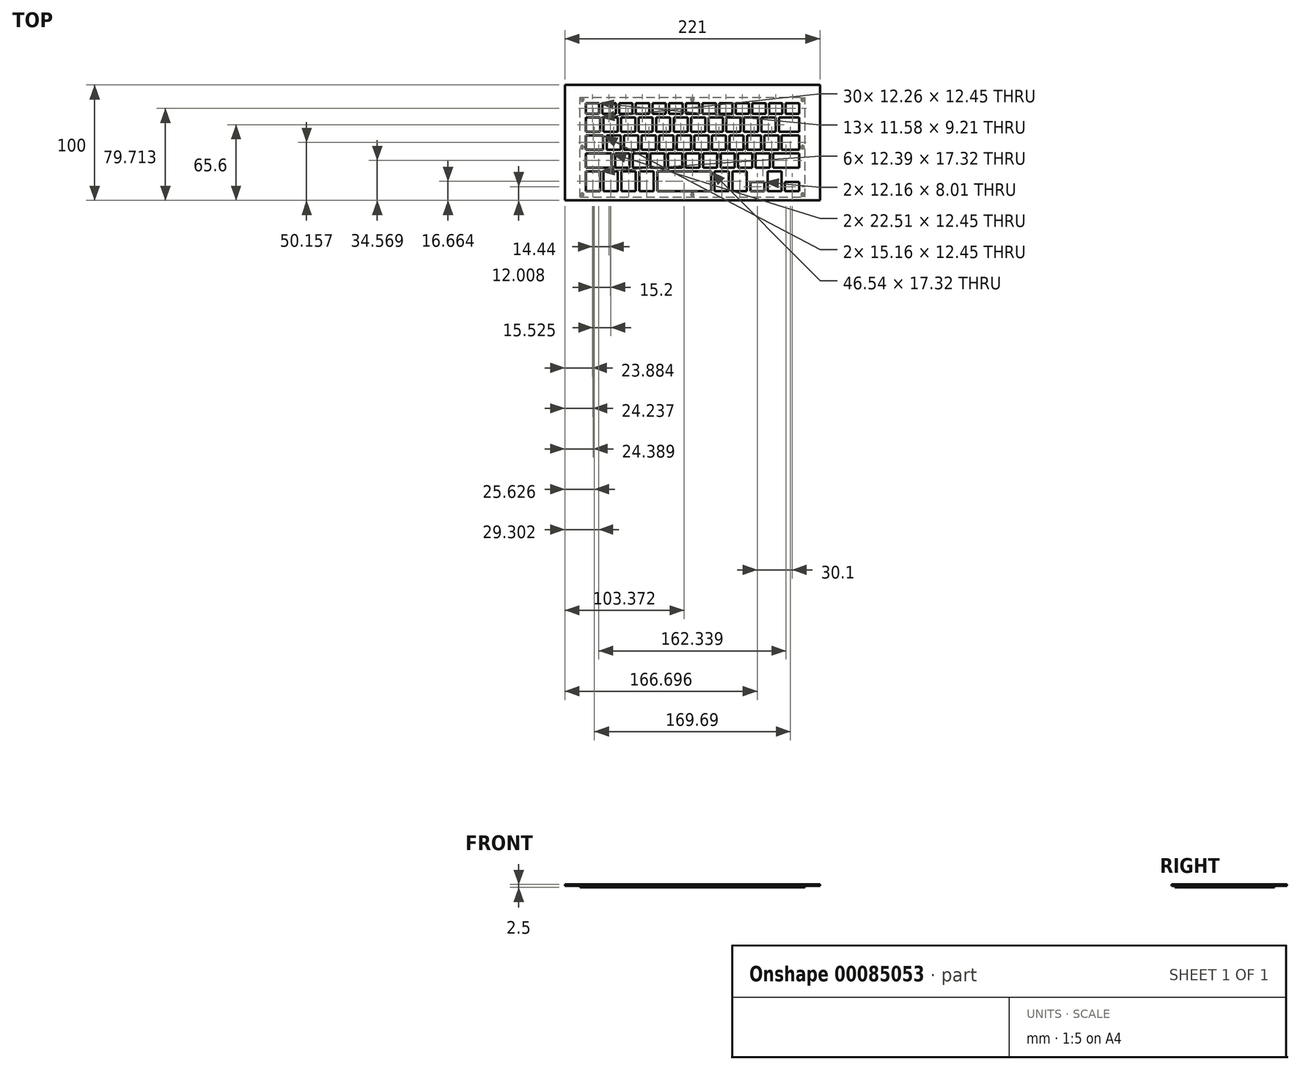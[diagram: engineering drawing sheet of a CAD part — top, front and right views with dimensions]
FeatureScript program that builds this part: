
annotation { "Feature Type Name" : "Feature", "Feature Type Description" : "" }
export const myFeature = defineFeature(function(context is Context, id is Id, definition is map)
    precondition{}
    {
        {
            var Q0;
            Q0=qCreatedBy(makeId("Top.planeOp"),FACE);
            var sketch = newSketch(context, id + "F0", { "sketchPlane" : qUnion([Q0])});
            skLineSegment(sketch, "E0", {"start": v(-92.4, 38.16) * mm, "end": v(-80.82, 38.16) * mm});
            skLineSegment(sketch, "E1", {"start": v(-92.4, 28.95) * mm, "end": v(-92.4, 38.16) * mm});
            skLineSegment(sketch, "E2", {"start": v(-80.82, 38.16) * mm, "end": v(-80.82, 28.95) * mm});
            skLineSegment(sketch, "E3", {"start": v(-80.82, 28.95) * mm, "end": v(-92.4, 28.95) * mm});
            skLineSegment(sketch, "E4", {"start": v(-77.97, 28.95) * mm, "end": v(-77.97, 38.16) * mm});
            skLineSegment(sketch, "E5", {"start": v(-66.38, 28.95) * mm, "end": v(-77.97, 28.95) * mm});
            skLineSegment(sketch, "E6", {"start": v(-66.38, 38.16) * mm, "end": v(-66.38, 28.95) * mm});
            skLineSegment(sketch, "E7", {"start": v(-77.97, 38.16) * mm, "end": v(-66.38, 38.16) * mm});
            skLineSegment(sketch, "E8", {"start": v(-63.53, 38.16) * mm, "end": v(-51.94, 38.16) * mm});
            skLineSegment(sketch, "E9", {"start": v(-63.53, 28.95) * mm, "end": v(-63.53, 38.16) * mm});
            skLineSegment(sketch, "E10", {"start": v(-51.94, 28.95) * mm, "end": v(-63.53, 28.95) * mm});
            skLineSegment(sketch, "E11", {"start": v(-51.94, 38.16) * mm, "end": v(-51.94, 28.95) * mm});
            skLineSegment(sketch, "E12", {"start": v(-49.09, 28.95) * mm, "end": v(-49.09, 38.16) * mm});
            skLineSegment(sketch, "E13", {"start": v(-37.5, 28.95) * mm, "end": v(-49.09, 28.95) * mm});
            skLineSegment(sketch, "E14", {"start": v(-37.5, 38.16) * mm, "end": v(-37.5, 28.95) * mm});
            skLineSegment(sketch, "E15", {"start": v(-49.09, 38.16) * mm, "end": v(-37.5, 38.16) * mm});
            skLineSegment(sketch, "E16", {"start": v(-34.65, 38.16) * mm, "end": v(-23.06, 38.16) * mm});
            skLineSegment(sketch, "E17", {"start": v(-34.65, 28.95) * mm, "end": v(-34.65, 38.16) * mm});
            skLineSegment(sketch, "E18", {"start": v(-23.06, 28.95) * mm, "end": v(-34.65, 28.95) * mm});
            skLineSegment(sketch, "E19", {"start": v(-23.06, 38.16) * mm, "end": v(-23.06, 28.95) * mm});
            skLineSegment(sketch, "E20", {"start": v(-20.2, 38.16) * mm, "end": v(-8.62, 38.16) * mm});
            skLineSegment(sketch, "E21", {"start": v(-20.2, 28.95) * mm, "end": v(-20.2, 38.16) * mm});
            skLineSegment(sketch, "E22", {"start": v(-8.62, 28.95) * mm, "end": v(-20.2, 28.95) * mm});
            skLineSegment(sketch, "E23", {"start": v(-8.62, 38.16) * mm, "end": v(-8.62, 28.95) * mm});
            skLineSegment(sketch, "E24", {"start": v(-5.77, 38.16) * mm, "end": v(5.82, 38.16) * mm});
            skLineSegment(sketch, "E25", {"start": v(-5.77, 28.95) * mm, "end": v(-5.77, 38.16) * mm});
            skLineSegment(sketch, "E26", {"start": v(5.82, 28.95) * mm, "end": v(-5.77, 28.95) * mm});
            skLineSegment(sketch, "E27", {"start": v(5.82, 38.16) * mm, "end": v(5.82, 28.95) * mm});
            skLineSegment(sketch, "E28", {"start": v(8.67, 38.16) * mm, "end": v(20.26, 38.16) * mm});
            skLineSegment(sketch, "E29", {"start": v(8.67, 28.95) * mm, "end": v(8.67, 38.16) * mm});
            skLineSegment(sketch, "E30", {"start": v(20.26, 28.95) * mm, "end": v(8.67, 28.95) * mm});
            skLineSegment(sketch, "E31", {"start": v(20.26, 38.16) * mm, "end": v(20.26, 28.95) * mm});
            skLineSegment(sketch, "E32", {"start": v(23.11, 38.16) * mm, "end": v(34.7, 38.16) * mm});
            skLineSegment(sketch, "E33", {"start": v(23.11, 28.95) * mm, "end": v(23.11, 38.16) * mm});
            skLineSegment(sketch, "E34", {"start": v(34.7, 28.95) * mm, "end": v(23.11, 28.95) * mm});
            skLineSegment(sketch, "E35", {"start": v(34.7, 38.16) * mm, "end": v(34.7, 28.95) * mm});
            skLineSegment(sketch, "E36", {"start": v(37.55, 38.16) * mm, "end": v(49.14, 38.16) * mm});
            skLineSegment(sketch, "E37", {"start": v(37.55, 28.95) * mm, "end": v(37.55, 38.16) * mm});
            skLineSegment(sketch, "E38", {"start": v(49.14, 28.95) * mm, "end": v(37.55, 28.95) * mm});
            skLineSegment(sketch, "E39", {"start": v(49.14, 38.16) * mm, "end": v(49.14, 28.95) * mm});
            skLineSegment(sketch, "E40", {"start": v(52, 38.16) * mm, "end": v(63.58, 38.16) * mm});
            skLineSegment(sketch, "E41", {"start": v(52, 28.95) * mm, "end": v(52, 38.16) * mm});
            skLineSegment(sketch, "E42", {"start": v(63.58, 28.95) * mm, "end": v(52, 28.95) * mm});
            skLineSegment(sketch, "E43", {"start": v(63.58, 38.16) * mm, "end": v(63.58, 28.95) * mm});
            skLineSegment(sketch, "E44", {"start": v(66.43, 38.16) * mm, "end": v(78.02, 38.16) * mm});
            skLineSegment(sketch, "E45", {"start": v(66.43, 28.95) * mm, "end": v(66.43, 38.16) * mm});
            skLineSegment(sketch, "E46", {"start": v(78.02, 28.95) * mm, "end": v(66.43, 28.95) * mm});
            skLineSegment(sketch, "E47", {"start": v(78.02, 38.16) * mm, "end": v(78.02, 28.95) * mm});
            skLineSegment(sketch, "E48", {"start": v(80.87, 38.16) * mm, "end": v(92.46, 38.16) * mm});
            skLineSegment(sketch, "E49", {"start": v(92.46, 38.16) * mm, "end": v(92.46, 28.95) * mm});
            skLineSegment(sketch, "E50", {"start": v(80.87, 28.95) * mm, "end": v(80.87, 38.16) * mm});
            skLineSegment(sketch, "E51", {"start": v(92.46, 28.95) * mm, "end": v(80.87, 28.95) * mm});
            skLineSegment(sketch, "E52", {"start": v(-92.24, 13.22) * mm, "end": v(-92.24, 25.66) * mm});
            skLineSegment(sketch, "E53", {"start": v(-92.24, 25.66) * mm, "end": v(-79.98, 25.66) * mm});
            skLineSegment(sketch, "E54", {"start": v(-79.98, 25.66) * mm, "end": v(-79.98, 13.22) * mm});
            skLineSegment(sketch, "E55", {"start": v(-79.98, 13.22) * mm, "end": v(-92.24, 13.22) * mm});
            skLineSegment(sketch, "E56", {"start": v(-77.04, 13.22) * mm, "end": v(-77.04, 25.66) * mm});
            skLineSegment(sketch, "E57", {"start": v(-77.04, 25.66) * mm, "end": v(-64.78, 25.66) * mm});
            skLineSegment(sketch, "E58", {"start": v(-64.78, 25.66) * mm, "end": v(-64.78, 13.22) * mm});
            skLineSegment(sketch, "E59", {"start": v(-64.78, 13.22) * mm, "end": v(-77.04, 13.22) * mm});
            skLineSegment(sketch, "E60", {"start": v(-61.84, 13.22) * mm, "end": v(-61.84, 25.66) * mm});
            skLineSegment(sketch, "E61", {"start": v(-61.84, 25.66) * mm, "end": v(-49.58, 25.66) * mm});
            skLineSegment(sketch, "E62", {"start": v(-49.58, 25.66) * mm, "end": v(-49.58, 13.22) * mm});
            skLineSegment(sketch, "E63", {"start": v(-49.58, 13.22) * mm, "end": v(-61.84, 13.22) * mm});
            skLineSegment(sketch, "E64", {"start": v(-46.64, 13.22) * mm, "end": v(-46.64, 25.66) * mm});
            skLineSegment(sketch, "E65", {"start": v(-46.64, 25.66) * mm, "end": v(-34.38, 25.66) * mm});
            skLineSegment(sketch, "E66", {"start": v(-34.38, 13.22) * mm, "end": v(-46.64, 13.22) * mm});
            skLineSegment(sketch, "E67", {"start": v(-34.38, 25.66) * mm, "end": v(-34.38, 13.22) * mm});
            skLineSegment(sketch, "E68", {"start": v(-31.44, 13.22) * mm, "end": v(-31.44, 25.66) * mm});
            skLineSegment(sketch, "E69", {"start": v(-19.18, 13.22) * mm, "end": v(-31.44, 13.22) * mm});
            skLineSegment(sketch, "E70", {"start": v(-19.18, 25.66) * mm, "end": v(-19.18, 13.22) * mm});
            skLineSegment(sketch, "E71", {"start": v(-31.44, 25.66) * mm, "end": v(-19.18, 25.66) * mm});
            skLineSegment(sketch, "E72", {"start": v(-16.24, 25.66) * mm, "end": v(-3.98, 25.66) * mm});
            skLineSegment(sketch, "E73", {"start": v(-1.04, 25.66) * mm, "end": v(11.22, 25.66) * mm});
            skLineSegment(sketch, "E74", {"start": v(14.16, 25.66) * mm, "end": v(26.42, 25.66) * mm});
            skLineSegment(sketch, "E75", {"start": v(-16.24, 13.22) * mm, "end": v(-16.24, 25.66) * mm});
            skLineSegment(sketch, "E76", {"start": v(-3.98, 25.66) * mm, "end": v(-3.98, 13.22) * mm});
            skLineSegment(sketch, "E77", {"start": v(-1.04, 13.22) * mm, "end": v(-1.04, 25.66) * mm});
            skLineSegment(sketch, "E78", {"start": v(11.22, 25.66) * mm, "end": v(11.22, 13.22) * mm});
            skLineSegment(sketch, "E79", {"start": v(14.16, 13.22) * mm, "end": v(14.16, 25.66) * mm});
            skLineSegment(sketch, "E80", {"start": v(26.42, 25.66) * mm, "end": v(26.42, 13.22) * mm});
            skLineSegment(sketch, "E81", {"start": v(26.42, 13.22) * mm, "end": v(14.16, 13.22) * mm});
            skLineSegment(sketch, "E82", {"start": v(11.22, 13.22) * mm, "end": v(-1.04, 13.22) * mm});
            skLineSegment(sketch, "E83", {"start": v(-3.98, 13.22) * mm, "end": v(-16.24, 13.22) * mm});
            skLineSegment(sketch, "E84", {"start": v(41.62, 13.22) * mm, "end": v(29.36, 13.22) * mm});
            skLineSegment(sketch, "E85", {"start": v(29.36, 13.22) * mm, "end": v(29.36, 25.66) * mm});
            skLineSegment(sketch, "E86", {"start": v(29.36, 25.66) * mm, "end": v(41.62, 25.66) * mm});
            skLineSegment(sketch, "E87", {"start": v(41.62, 25.66) * mm, "end": v(41.62, 13.22) * mm});
            skLineSegment(sketch, "E88", {"start": v(44.56, 13.22) * mm, "end": v(44.56, 25.66) * mm});
            skLineSegment(sketch, "E89", {"start": v(44.56, 25.66) * mm, "end": v(56.82, 25.66) * mm});
            skLineSegment(sketch, "E90", {"start": v(56.82, 25.66) * mm, "end": v(56.82, 13.22) * mm});
            skLineSegment(sketch, "E91", {"start": v(56.82, 13.22) * mm, "end": v(44.56, 13.22) * mm});
            skLineSegment(sketch, "E92", {"start": v(59.76, 13.22) * mm, "end": v(59.76, 25.66) * mm});
            skLineSegment(sketch, "E93", {"start": v(59.76, 25.66) * mm, "end": v(72.02, 25.66) * mm});
            skLineSegment(sketch, "E94", {"start": v(72.02, 25.66) * mm, "end": v(72.02, 13.22) * mm});
            skLineSegment(sketch, "E95", {"start": v(72.02, 13.22) * mm, "end": v(59.76, 13.22) * mm});
            skLineSegment(sketch, "E96", {"start": v(92.4, 13.22) * mm, "end": v(75.1, 13.22) * mm});
            skLineSegment(sketch, "E97", {"start": v(75.1, 13.22) * mm, "end": v(75.1, 25.66) * mm});
            skLineSegment(sketch, "E98", {"start": v(75.1, 25.66) * mm, "end": v(92.4, 25.66) * mm});
            skLineSegment(sketch, "E99", {"start": v(92.4, 25.66) * mm, "end": v(92.4, 13.22) * mm});
            skLineSegment(sketch, "E100", {"start": v(92.4, 10.22) * mm, "end": v(92.4, -2.23) * mm});
            skLineSegment(sketch, "E101", {"start": v(92.4, -5.37) * mm, "end": v(92.4, -17.81) * mm});
            skLineSegment(sketch, "E102", {"start": v(77.23, 10.22) * mm, "end": v(92.4, 10.22) * mm});
            skLineSegment(sketch, "E103", {"start": v(77.23, -2.23) * mm, "end": v(77.23, 10.22) * mm});
            skLineSegment(sketch, "E104", {"start": v(92.4, -2.23) * mm, "end": v(77.23, -2.23) * mm});
            skLineSegment(sketch, "E105", {"start": v(69.88, -5.37) * mm, "end": v(92.4, -5.37) * mm});
            skLineSegment(sketch, "E106", {"start": v(69.88, -17.81) * mm, "end": v(69.88, -5.37) * mm});
            skLineSegment(sketch, "E107", {"start": v(92.4, -17.81) * mm, "end": v(69.88, -17.81) * mm});
            skLineSegment(sketch, "E108", {"start": v(-92.46, 10.22) * mm, "end": v(-77.3, 10.22) * mm});
            skLineSegment(sketch, "E109", {"start": v(-92.46, -2.23) * mm, "end": v(-92.46, 10.22) * mm});
            skLineSegment(sketch, "E110", {"start": v(-77.3, -2.23) * mm, "end": v(-92.46, -2.23) * mm});
            skLineSegment(sketch, "E111", {"start": v(-77.3, 10.22) * mm, "end": v(-77.3, -2.23) * mm});
            skLineSegment(sketch, "E112", {"start": v(-92.46, -5.37) * mm, "end": v(-69.94, -5.37) * mm});
            skLineSegment(sketch, "E113", {"start": v(-92.46, -17.81) * mm, "end": v(-92.46, -5.37) * mm});
            skLineSegment(sketch, "E114", {"start": v(-69.94, -17.81) * mm, "end": v(-92.46, -17.81) * mm});
            skLineSegment(sketch, "E115", {"start": v(-69.94, -5.37) * mm, "end": v(-69.94, -17.81) * mm});
            skLineSegment(sketch, "E116", {"start": v(-74.35, -2.23) * mm, "end": v(-74.35, 10.22) * mm});
            skLineSegment(sketch, "E117", {"start": v(-74.35, 10.22) * mm, "end": v(-62.09, 10.22) * mm});
            skLineSegment(sketch, "E118", {"start": v(-62.09, 10.22) * mm, "end": v(-62.09, -2.23) * mm});
            skLineSegment(sketch, "E119", {"start": v(-62.09, -2.23) * mm, "end": v(-74.35, -2.23) * mm});
            skLineSegment(sketch, "E120", {"start": v(-59.15, -2.23) * mm, "end": v(-59.15, 10.22) * mm});
            skLineSegment(sketch, "E121", {"start": v(-59.15, 10.22) * mm, "end": v(-46.89, 10.22) * mm});
            skLineSegment(sketch, "E122", {"start": v(-46.89, 10.22) * mm, "end": v(-46.89, -2.23) * mm});
            skLineSegment(sketch, "E123", {"start": v(-46.89, -2.23) * mm, "end": v(-59.15, -2.23) * mm});
            skLineSegment(sketch, "E124", {"start": v(-43.95, -2.23) * mm, "end": v(-43.95, 10.22) * mm});
            skLineSegment(sketch, "E125", {"start": v(-31.69, -2.23) * mm, "end": v(-43.95, -2.23) * mm});
            skLineSegment(sketch, "E126", {"start": v(-31.69, 10.22) * mm, "end": v(-31.69, -2.23) * mm});
            skLineSegment(sketch, "E127", {"start": v(-43.95, 10.22) * mm, "end": v(-31.69, 10.22) * mm});
            skLineSegment(sketch, "E128", {"start": v(-28.75, -2.23) * mm, "end": v(-28.75, 10.22) * mm});
            skLineSegment(sketch, "E129", {"start": v(-28.75, 10.22) * mm, "end": v(-16.49, 10.22) * mm});
            skLineSegment(sketch, "E130", {"start": v(-16.49, 10.22) * mm, "end": v(-16.49, -2.23) * mm});
            skLineSegment(sketch, "E131", {"start": v(-16.49, -2.23) * mm, "end": v(-28.75, -2.23) * mm});
            skLineSegment(sketch, "E132", {"start": v(-13.55, -2.23) * mm, "end": v(-13.55, 10.22) * mm});
            skLineSegment(sketch, "E133", {"start": v(-13.55, 10.22) * mm, "end": v(-1.29, 10.22) * mm});
            skLineSegment(sketch, "E134", {"start": v(-1.29, 10.22) * mm, "end": v(-1.29, -2.23) * mm});
            skLineSegment(sketch, "E135", {"start": v(-1.29, -2.23) * mm, "end": v(-13.55, -2.23) * mm});
            skLineSegment(sketch, "E136", {"start": v(1.65, -2.23) * mm, "end": v(1.65, 10.22) * mm});
            skLineSegment(sketch, "E137", {"start": v(1.65, 10.22) * mm, "end": v(13.91, 10.22) * mm});
            skLineSegment(sketch, "E138", {"start": v(13.91, 10.22) * mm, "end": v(13.91, -2.23) * mm});
            skLineSegment(sketch, "E139", {"start": v(13.91, -2.23) * mm, "end": v(1.65, -2.23) * mm});
            skLineSegment(sketch, "E140", {"start": v(16.85, -2.23) * mm, "end": v(16.85, 10.22) * mm});
            skLineSegment(sketch, "E141", {"start": v(16.85, 10.22) * mm, "end": v(29.11, 10.22) * mm});
            skLineSegment(sketch, "E142", {"start": v(29.11, 10.22) * mm, "end": v(29.11, -2.23) * mm});
            skLineSegment(sketch, "E143", {"start": v(29.11, -2.23) * mm, "end": v(16.85, -2.23) * mm});
            skLineSegment(sketch, "E144", {"start": v(32.05, -2.23) * mm, "end": v(32.05, 10.22) * mm});
            skLineSegment(sketch, "E145", {"start": v(32.05, 10.22) * mm, "end": v(44.31, 10.22) * mm});
            skLineSegment(sketch, "E146", {"start": v(44.31, 10.22) * mm, "end": v(44.31, -2.23) * mm});
            skLineSegment(sketch, "E147", {"start": v(44.31, -2.23) * mm, "end": v(32.05, -2.23) * mm});
            skLineSegment(sketch, "E148", {"start": v(47.25, -2.23) * mm, "end": v(47.25, 10.22) * mm});
            skLineSegment(sketch, "E149", {"start": v(47.25, 10.22) * mm, "end": v(59.51, 10.22) * mm});
            skLineSegment(sketch, "E150", {"start": v(59.51, 10.22) * mm, "end": v(59.51, -2.23) * mm});
            skLineSegment(sketch, "E151", {"start": v(59.51, -2.23) * mm, "end": v(47.25, -2.23) * mm});
            skLineSegment(sketch, "E152", {"start": v(62.45, -2.23) * mm, "end": v(62.45, 10.22) * mm});
            skLineSegment(sketch, "E153", {"start": v(62.45, 10.22) * mm, "end": v(74.71, 10.22) * mm});
            skLineSegment(sketch, "E154", {"start": v(74.71, 10.22) * mm, "end": v(74.71, -2.23) * mm});
            skLineSegment(sketch, "E155", {"start": v(74.71, -2.23) * mm, "end": v(62.45, -2.23) * mm});
            skLineSegment(sketch, "E156", {"start": v(-66.8, -17.81) * mm, "end": v(-66.8, -5.37) * mm});
            skLineSegment(sketch, "E157", {"start": v(-54.54, -5.37) * mm, "end": v(-54.54, -17.81) * mm});
            skLineSegment(sketch, "E158", {"start": v(-51.6, -17.81) * mm, "end": v(-51.6, -5.37) * mm});
            skLineSegment(sketch, "E159", {"start": v(-39.34, -5.37) * mm, "end": v(-39.34, -17.81) * mm});
            skLineSegment(sketch, "E160", {"start": v(-36.4, -17.81) * mm, "end": v(-36.4, -5.37) * mm});
            skLineSegment(sketch, "E161", {"start": v(-24.14, -5.37) * mm, "end": v(-24.14, -17.81) * mm});
            skLineSegment(sketch, "E162", {"start": v(-21.2, -17.81) * mm, "end": v(-21.2, -5.37) * mm});
            skLineSegment(sketch, "E163", {"start": v(-8.94, -5.37) * mm, "end": v(-8.94, -17.81) * mm});
            skLineSegment(sketch, "E164", {"start": v(-6, -17.81) * mm, "end": v(-6, -5.37) * mm});
            skLineSegment(sketch, "E165", {"start": v(6.26, -5.37) * mm, "end": v(6.26, -17.81) * mm});
            skLineSegment(sketch, "E166", {"start": v(9.2, -17.81) * mm, "end": v(9.2, -5.37) * mm});
            skLineSegment(sketch, "E167", {"start": v(21.46, -5.37) * mm, "end": v(21.46, -17.81) * mm});
            skLineSegment(sketch, "E168", {"start": v(24.4, -17.81) * mm, "end": v(24.4, -5.37) * mm});
            skLineSegment(sketch, "E169", {"start": v(36.66, -5.37) * mm, "end": v(36.66, -17.81) * mm});
            skLineSegment(sketch, "E170", {"start": v(39.6, -17.81) * mm, "end": v(39.6, -5.37) * mm});
            skLineSegment(sketch, "E171", {"start": v(51.86, -5.37) * mm, "end": v(51.86, -17.81) * mm});
            skLineSegment(sketch, "E172", {"start": v(54.8, -17.81) * mm, "end": v(54.8, -5.37) * mm});
            skLineSegment(sketch, "E173", {"start": v(67.06, -5.37) * mm, "end": v(67.06, -17.81) * mm});
            skLineSegment(sketch, "E174", {"start": v(54.8, -5.37) * mm, "end": v(67.06, -5.37) * mm});
            skLineSegment(sketch, "E175", {"start": v(39.6, -5.37) * mm, "end": v(51.86, -5.37) * mm});
            skLineSegment(sketch, "E176", {"start": v(24.4, -5.37) * mm, "end": v(36.66, -5.37) * mm});
            skLineSegment(sketch, "E177", {"start": v(9.2, -5.37) * mm, "end": v(21.46, -5.37) * mm});
            skLineSegment(sketch, "E178", {"start": v(-6, -5.37) * mm, "end": v(6.26, -5.37) * mm});
            skLineSegment(sketch, "E179", {"start": v(-21.2, -5.37) * mm, "end": v(-8.94, -5.37) * mm});
            skLineSegment(sketch, "E180", {"start": v(-36.4, -5.37) * mm, "end": v(-24.14, -5.37) * mm});
            skLineSegment(sketch, "E181", {"start": v(-51.6, -5.37) * mm, "end": v(-39.34, -5.37) * mm});
            skLineSegment(sketch, "E182", {"start": v(-66.8, -5.37) * mm, "end": v(-54.54, -5.37) * mm});
            skLineSegment(sketch, "E183", {"start": v(-54.54, -17.81) * mm, "end": v(-66.8, -17.81) * mm});
            skLineSegment(sketch, "E184", {"start": v(-39.34, -17.81) * mm, "end": v(-51.6, -17.81) * mm});
            skLineSegment(sketch, "E185", {"start": v(-24.14, -17.81) * mm, "end": v(-36.4, -17.81) * mm});
            skLineSegment(sketch, "E186", {"start": v(-8.94, -17.81) * mm, "end": v(-21.2, -17.81) * mm});
            skLineSegment(sketch, "E187", {"start": v(6.26, -17.81) * mm, "end": v(-6, -17.81) * mm});
            skLineSegment(sketch, "E188", {"start": v(21.46, -17.81) * mm, "end": v(9.2, -17.81) * mm});
            skLineSegment(sketch, "E189", {"start": v(36.66, -17.81) * mm, "end": v(24.4, -17.81) * mm});
            skLineSegment(sketch, "E190", {"start": v(51.86, -17.81) * mm, "end": v(39.6, -17.81) * mm});
            skLineSegment(sketch, "E191", {"start": v(67.06, -17.81) * mm, "end": v(54.8, -17.81) * mm});
            skLineSegment(sketch, "E192", {"start": v(-80.07, -20.84) * mm, "end": v(-92.46, -20.84) * mm});
            skLineSegment(sketch, "E193", {"start": v(-92.46, -38.16) * mm, "end": v(-80.07, -38.16) * mm});
            skLineSegment(sketch, "E194", {"start": v(-80.07, -38.16) * mm, "end": v(-80.07, -20.84) * mm});
            skLineSegment(sketch, "E195", {"start": v(-76.93, -20.84) * mm, "end": v(-76.93, -38.16) * mm});
            skLineSegment(sketch, "E196", {"start": v(-64.54, -20.84) * mm, "end": v(-76.93, -20.84) * mm});
            skLineSegment(sketch, "E197", {"start": v(-64.54, -38.16) * mm, "end": v(-64.54, -20.84) * mm});
            skLineSegment(sketch, "E198", {"start": v(-76.93, -38.16) * mm, "end": v(-64.54, -38.16) * mm});
            skLineSegment(sketch, "E199", {"start": v(-61.4, -38.16) * mm, "end": v(-49.02, -38.16) * mm});
            skLineSegment(sketch, "E200", {"start": v(-61.4, -20.84) * mm, "end": v(-61.4, -38.16) * mm});
            skLineSegment(sketch, "E201", {"start": v(-49.02, -38.16) * mm, "end": v(-49.02, -20.84) * mm});
            skLineSegment(sketch, "E202", {"start": v(-49.02, -20.84) * mm, "end": v(-61.4, -20.84) * mm});
            skLineSegment(sketch, "E203", {"start": v(-45.88, -20.84) * mm, "end": v(-45.88, -38.16) * mm});
            skLineSegment(sketch, "E204", {"start": v(-33.5, -20.84) * mm, "end": v(-45.88, -20.84) * mm});
            skLineSegment(sketch, "E205", {"start": v(-33.5, -38.16) * mm, "end": v(-33.5, -20.84) * mm});
            skLineSegment(sketch, "E206", {"start": v(-45.88, -38.16) * mm, "end": v(-33.5, -38.16) * mm});
            skLineSegment(sketch, "E207", {"start": v(16.14, -38.16) * mm, "end": v(-30.4, -38.16) * mm});
            skLineSegment(sketch, "E208", {"start": v(-30.4, -38.16) * mm, "end": v(-30.4, -20.84) * mm});
            skLineSegment(sketch, "E209", {"start": v(-30.4, -20.84) * mm, "end": v(16.14, -20.84) * mm});
            skLineSegment(sketch, "E210", {"start": v(16.14, -20.84) * mm, "end": v(16.14, -38.16) * mm});
            skLineSegment(sketch, "E211", {"start": v(19.24, -38.16) * mm, "end": v(19.24, -20.84) * mm});
            skLineSegment(sketch, "E212", {"start": v(19.24, -20.84) * mm, "end": v(31.63, -20.84) * mm});
            skLineSegment(sketch, "E213", {"start": v(31.63, -20.84) * mm, "end": v(31.63, -38.16) * mm});
            skLineSegment(sketch, "E214", {"start": v(31.63, -38.16) * mm, "end": v(19.24, -38.16) * mm});
            skLineSegment(sketch, "E215", {"start": v(47.15, -38.16) * mm, "end": v(34.76, -38.16) * mm});
            skLineSegment(sketch, "E216", {"start": v(34.76, -38.16) * mm, "end": v(34.76, -20.84) * mm});
            skLineSegment(sketch, "E217", {"start": v(34.76, -20.84) * mm, "end": v(47.15, -20.84) * mm});
            skLineSegment(sketch, "E218", {"start": v(47.15, -20.84) * mm, "end": v(47.15, -38.16) * mm});
            skLineSegment(sketch, "E219", {"start": v(62.27, -38.16) * mm, "end": v(50.12, -38.16) * mm});
            skLineSegment(sketch, "E220", {"start": v(50.12, -38.16) * mm, "end": v(50.12, -30.15) * mm});
            skLineSegment(sketch, "E221", {"start": v(50.12, -30.15) * mm, "end": v(62.27, -30.15) * mm});
            skLineSegment(sketch, "E222", {"start": v(62.27, -30.15) * mm, "end": v(62.27, -38.16) * mm});
            skLineSegment(sketch, "E223", {"start": v(77.32, -38.16) * mm, "end": v(65.17, -38.16) * mm});
            skLineSegment(sketch, "E224", {"start": v(65.17, -20.84) * mm, "end": v(77.32, -20.84) * mm});
            skLineSegment(sketch, "E225", {"start": v(80.22, -30.15) * mm, "end": v(92.37, -30.15) * mm});
            skLineSegment(sketch, "E226", {"start": v(80.22, -38.16) * mm, "end": v(80.22, -30.15) * mm});
            skLineSegment(sketch, "E227", {"start": v(92.37, -38.16) * mm, "end": v(80.22, -38.16) * mm});
            skLineSegment(sketch, "E228", {"start": v(92.37, -30.15) * mm, "end": v(92.37, -38.16) * mm});
            skLineSegment(sketch, "E229", {"start": v(65.17, -20.84) * mm, "end": v(65.17, -38.16) * mm});
            skLineSegment(sketch, "E230", {"start": v(77.32, -38.16) * mm, "end": v(77.32, -20.84) * mm});
            skLineSegment(sketch, "E231", {"start": v(-92.46, -20.84) * mm, "end": v(-92.46, -38.16) * mm});
            skPoint(sketch, "E232.middle", {"position": v(0, 0) * mm});
            skLineSegment(sketch, "E233", {"start": v(-110.5, -46.16) * mm, "end": v(110.5, -46.16) * mm});
            skLineSegment(sketch, "E234", {"start": v(110.5, -46.16) * mm, "end": v(110.5, 53.84) * mm});
            skLineSegment(sketch, "E235", {"start": v(110.5, 53.84) * mm, "end": v(-110.5, 53.84) * mm});
            skLineSegment(sketch, "E236", {"start": v(-110.5, 53.84) * mm, "end": v(-110.5, -46.16) * mm});
            skLineSegment(sketch, "E237", {"start": v(0, 0) * mm, "end": v(0, -46.16) * mm, "construction": true});
            skSolve(sketch);
        }
        {
            var Q0;
            Q0=makeQuery(id+"F0.imprint","IMPRINT",FACE,{"disambiguationData":[TD([[makeQuery(id+"F0.imprint","IMPRINT",EDGE,{"derivedFrom":sQuery(id+"F0.wireOp",EDGE,"E0")}),1.0]])]});
            extrude(context, id + "F1", {"entities" : qUnion([Q0]), "depth" : 1 * mm, "hasDraft" : true, "draftAngle" : 0 * degree, "draftPullDirection" : true});
        }
        {
            var Q0;
            Q0=makeQuery(id+"F1.opExtrude","CAP_FACE",FACE,{"disambiguationData":[OSD([sQuery(id+"F0.wireOp",EDGE,"E0"),sQuery(id+"F0.wireOp",EDGE,"E1"),sQuery(id+"F0.wireOp",EDGE,"E2"),sQuery(id+"F0.wireOp",EDGE,"E3"),sQuery(id+"F0.wireOp",EDGE,"E4"),sQuery(id+"F0.wireOp",EDGE,"E5"),sQuery(id+"F0.wireOp",EDGE,"E6"),sQuery(id+"F0.wireOp",EDGE,"E7"),sQuery(id+"F0.wireOp",EDGE,"E8"),sQuery(id+"F0.wireOp",EDGE,"E9"),sQuery(id+"F0.wireOp",EDGE,"E10"),sQuery(id+"F0.wireOp",EDGE,"E11"),sQuery(id+"F0.wireOp",EDGE,"E12"),sQuery(id+"F0.wireOp",EDGE,"E13"),sQuery(id+"F0.wireOp",EDGE,"E14"),sQuery(id+"F0.wireOp",EDGE,"E15"),sQuery(id+"F0.wireOp",EDGE,"E16"),sQuery(id+"F0.wireOp",EDGE,"E17"),sQuery(id+"F0.wireOp",EDGE,"E18"),sQuery(id+"F0.wireOp",EDGE,"E19"),sQuery(id+"F0.wireOp",EDGE,"E20"),sQuery(id+"F0.wireOp",EDGE,"E21"),sQuery(id+"F0.wireOp",EDGE,"E22"),sQuery(id+"F0.wireOp",EDGE,"E23"),sQuery(id+"F0.wireOp",EDGE,"E24"),sQuery(id+"F0.wireOp",EDGE,"E25"),sQuery(id+"F0.wireOp",EDGE,"E26"),sQuery(id+"F0.wireOp",EDGE,"E27"),sQuery(id+"F0.wireOp",EDGE,"E28"),sQuery(id+"F0.wireOp",EDGE,"E29"),sQuery(id+"F0.wireOp",EDGE,"E30"),sQuery(id+"F0.wireOp",EDGE,"E31"),sQuery(id+"F0.wireOp",EDGE,"E32"),sQuery(id+"F0.wireOp",EDGE,"E33"),sQuery(id+"F0.wireOp",EDGE,"E34"),sQuery(id+"F0.wireOp",EDGE,"E35"),sQuery(id+"F0.wireOp",EDGE,"E36"),sQuery(id+"F0.wireOp",EDGE,"E37"),sQuery(id+"F0.wireOp",EDGE,"E38"),sQuery(id+"F0.wireOp",EDGE,"E39"),sQuery(id+"F0.wireOp",EDGE,"E40"),sQuery(id+"F0.wireOp",EDGE,"E41"),sQuery(id+"F0.wireOp",EDGE,"E42"),sQuery(id+"F0.wireOp",EDGE,"E43"),sQuery(id+"F0.wireOp",EDGE,"E44"),sQuery(id+"F0.wireOp",EDGE,"E45"),sQuery(id+"F0.wireOp",EDGE,"E46"),sQuery(id+"F0.wireOp",EDGE,"E47"),sQuery(id+"F0.wireOp",EDGE,"E48"),sQuery(id+"F0.wireOp",EDGE,"E49"),sQuery(id+"F0.wireOp",EDGE,"E50"),sQuery(id+"F0.wireOp",EDGE,"E51"),sQuery(id+"F0.wireOp",EDGE,"E52"),sQuery(id+"F0.wireOp",EDGE,"E53"),sQuery(id+"F0.wireOp",EDGE,"E54"),sQuery(id+"F0.wireOp",EDGE,"E55"),sQuery(id+"F0.wireOp",EDGE,"E56"),sQuery(id+"F0.wireOp",EDGE,"E57"),sQuery(id+"F0.wireOp",EDGE,"E58"),sQuery(id+"F0.wireOp",EDGE,"E59"),sQuery(id+"F0.wireOp",EDGE,"E60"),sQuery(id+"F0.wireOp",EDGE,"E61"),sQuery(id+"F0.wireOp",EDGE,"E62"),sQuery(id+"F0.wireOp",EDGE,"E63"),sQuery(id+"F0.wireOp",EDGE,"E64"),sQuery(id+"F0.wireOp",EDGE,"E65"),sQuery(id+"F0.wireOp",EDGE,"E66"),sQuery(id+"F0.wireOp",EDGE,"E67"),sQuery(id+"F0.wireOp",EDGE,"E68"),sQuery(id+"F0.wireOp",EDGE,"E69"),sQuery(id+"F0.wireOp",EDGE,"E70"),sQuery(id+"F0.wireOp",EDGE,"E71"),sQuery(id+"F0.wireOp",EDGE,"E72"),sQuery(id+"F0.wireOp",EDGE,"E73"),sQuery(id+"F0.wireOp",EDGE,"E74"),sQuery(id+"F0.wireOp",EDGE,"E75"),sQuery(id+"F0.wireOp",EDGE,"E76"),sQuery(id+"F0.wireOp",EDGE,"E77"),sQuery(id+"F0.wireOp",EDGE,"E78"),sQuery(id+"F0.wireOp",EDGE,"E79"),sQuery(id+"F0.wireOp",EDGE,"E80"),sQuery(id+"F0.wireOp",EDGE,"E81"),sQuery(id+"F0.wireOp",EDGE,"E82"),sQuery(id+"F0.wireOp",EDGE,"E83"),sQuery(id+"F0.wireOp",EDGE,"E84"),sQuery(id+"F0.wireOp",EDGE,"E85"),sQuery(id+"F0.wireOp",EDGE,"E86"),sQuery(id+"F0.wireOp",EDGE,"E87"),sQuery(id+"F0.wireOp",EDGE,"E88"),sQuery(id+"F0.wireOp",EDGE,"E89"),sQuery(id+"F0.wireOp",EDGE,"E90"),sQuery(id+"F0.wireOp",EDGE,"E91"),sQuery(id+"F0.wireOp",EDGE,"E92"),sQuery(id+"F0.wireOp",EDGE,"E93"),sQuery(id+"F0.wireOp",EDGE,"E94"),sQuery(id+"F0.wireOp",EDGE,"E95"),sQuery(id+"F0.wireOp",EDGE,"E96"),sQuery(id+"F0.wireOp",EDGE,"E97"),sQuery(id+"F0.wireOp",EDGE,"E98"),sQuery(id+"F0.wireOp",EDGE,"E99"),sQuery(id+"F0.wireOp",EDGE,"E100"),sQuery(id+"F0.wireOp",EDGE,"E101"),sQuery(id+"F0.wireOp",EDGE,"E102"),sQuery(id+"F0.wireOp",EDGE,"E103"),sQuery(id+"F0.wireOp",EDGE,"E104"),sQuery(id+"F0.wireOp",EDGE,"E105"),sQuery(id+"F0.wireOp",EDGE,"E106"),sQuery(id+"F0.wireOp",EDGE,"E107"),sQuery(id+"F0.wireOp",EDGE,"E108"),sQuery(id+"F0.wireOp",EDGE,"E109"),sQuery(id+"F0.wireOp",EDGE,"E110"),sQuery(id+"F0.wireOp",EDGE,"E111"),sQuery(id+"F0.wireOp",EDGE,"E112"),sQuery(id+"F0.wireOp",EDGE,"E113"),sQuery(id+"F0.wireOp",EDGE,"E114"),sQuery(id+"F0.wireOp",EDGE,"E115"),sQuery(id+"F0.wireOp",EDGE,"E116"),sQuery(id+"F0.wireOp",EDGE,"E117"),sQuery(id+"F0.wireOp",EDGE,"E118"),sQuery(id+"F0.wireOp",EDGE,"E119"),sQuery(id+"F0.wireOp",EDGE,"E120"),sQuery(id+"F0.wireOp",EDGE,"E121"),sQuery(id+"F0.wireOp",EDGE,"E122"),sQuery(id+"F0.wireOp",EDGE,"E123"),sQuery(id+"F0.wireOp",EDGE,"E124"),sQuery(id+"F0.wireOp",EDGE,"E125"),sQuery(id+"F0.wireOp",EDGE,"E126"),sQuery(id+"F0.wireOp",EDGE,"E127"),sQuery(id+"F0.wireOp",EDGE,"E128"),sQuery(id+"F0.wireOp",EDGE,"E129"),sQuery(id+"F0.wireOp",EDGE,"E130"),sQuery(id+"F0.wireOp",EDGE,"E131"),sQuery(id+"F0.wireOp",EDGE,"E132"),sQuery(id+"F0.wireOp",EDGE,"E133"),sQuery(id+"F0.wireOp",EDGE,"E134"),sQuery(id+"F0.wireOp",EDGE,"E135"),sQuery(id+"F0.wireOp",EDGE,"E136"),sQuery(id+"F0.wireOp",EDGE,"E137"),sQuery(id+"F0.wireOp",EDGE,"E138"),sQuery(id+"F0.wireOp",EDGE,"E139"),sQuery(id+"F0.wireOp",EDGE,"E140"),sQuery(id+"F0.wireOp",EDGE,"E141"),sQuery(id+"F0.wireOp",EDGE,"E142"),sQuery(id+"F0.wireOp",EDGE,"E143"),sQuery(id+"F0.wireOp",EDGE,"E144"),sQuery(id+"F0.wireOp",EDGE,"E145"),sQuery(id+"F0.wireOp",EDGE,"E146"),sQuery(id+"F0.wireOp",EDGE,"E147"),sQuery(id+"F0.wireOp",EDGE,"E148"),sQuery(id+"F0.wireOp",EDGE,"E149"),sQuery(id+"F0.wireOp",EDGE,"E150"),sQuery(id+"F0.wireOp",EDGE,"E151"),sQuery(id+"F0.wireOp",EDGE,"E152"),sQuery(id+"F0.wireOp",EDGE,"E153"),sQuery(id+"F0.wireOp",EDGE,"E154"),sQuery(id+"F0.wireOp",EDGE,"E155"),sQuery(id+"F0.wireOp",EDGE,"E156"),sQuery(id+"F0.wireOp",EDGE,"E157"),sQuery(id+"F0.wireOp",EDGE,"E158"),sQuery(id+"F0.wireOp",EDGE,"E159"),sQuery(id+"F0.wireOp",EDGE,"E160"),sQuery(id+"F0.wireOp",EDGE,"E161"),sQuery(id+"F0.wireOp",EDGE,"E162"),sQuery(id+"F0.wireOp",EDGE,"E163"),sQuery(id+"F0.wireOp",EDGE,"E164"),sQuery(id+"F0.wireOp",EDGE,"E165"),sQuery(id+"F0.wireOp",EDGE,"E166"),sQuery(id+"F0.wireOp",EDGE,"E167"),sQuery(id+"F0.wireOp",EDGE,"E168"),sQuery(id+"F0.wireOp",EDGE,"E169"),sQuery(id+"F0.wireOp",EDGE,"E170"),sQuery(id+"F0.wireOp",EDGE,"E171"),sQuery(id+"F0.wireOp",EDGE,"E172"),sQuery(id+"F0.wireOp",EDGE,"E173"),sQuery(id+"F0.wireOp",EDGE,"E174"),sQuery(id+"F0.wireOp",EDGE,"E175"),sQuery(id+"F0.wireOp",EDGE,"E176"),sQuery(id+"F0.wireOp",EDGE,"E177"),sQuery(id+"F0.wireOp",EDGE,"E178"),sQuery(id+"F0.wireOp",EDGE,"E179"),sQuery(id+"F0.wireOp",EDGE,"E180"),sQuery(id+"F0.wireOp",EDGE,"E181"),sQuery(id+"F0.wireOp",EDGE,"E182"),sQuery(id+"F0.wireOp",EDGE,"E183"),sQuery(id+"F0.wireOp",EDGE,"E184"),sQuery(id+"F0.wireOp",EDGE,"E185"),sQuery(id+"F0.wireOp",EDGE,"E186"),sQuery(id+"F0.wireOp",EDGE,"E187"),sQuery(id+"F0.wireOp",EDGE,"E188"),sQuery(id+"F0.wireOp",EDGE,"E189"),sQuery(id+"F0.wireOp",EDGE,"E190"),sQuery(id+"F0.wireOp",EDGE,"E191"),sQuery(id+"F0.wireOp",EDGE,"E192"),sQuery(id+"F0.wireOp",EDGE,"E193"),sQuery(id+"F0.wireOp",EDGE,"E194"),sQuery(id+"F0.wireOp",EDGE,"E195"),sQuery(id+"F0.wireOp",EDGE,"E196"),sQuery(id+"F0.wireOp",EDGE,"E197"),sQuery(id+"F0.wireOp",EDGE,"E198"),sQuery(id+"F0.wireOp",EDGE,"E199"),sQuery(id+"F0.wireOp",EDGE,"E200"),sQuery(id+"F0.wireOp",EDGE,"E201"),sQuery(id+"F0.wireOp",EDGE,"E202"),sQuery(id+"F0.wireOp",EDGE,"E203"),sQuery(id+"F0.wireOp",EDGE,"E204"),sQuery(id+"F0.wireOp",EDGE,"E205"),sQuery(id+"F0.wireOp",EDGE,"E206"),sQuery(id+"F0.wireOp",EDGE,"E207"),sQuery(id+"F0.wireOp",EDGE,"E208"),sQuery(id+"F0.wireOp",EDGE,"E209"),sQuery(id+"F0.wireOp",EDGE,"E210"),sQuery(id+"F0.wireOp",EDGE,"E211"),sQuery(id+"F0.wireOp",EDGE,"E212"),sQuery(id+"F0.wireOp",EDGE,"E213"),sQuery(id+"F0.wireOp",EDGE,"E214"),sQuery(id+"F0.wireOp",EDGE,"E215"),sQuery(id+"F0.wireOp",EDGE,"E216"),sQuery(id+"F0.wireOp",EDGE,"E217"),sQuery(id+"F0.wireOp",EDGE,"E218"),sQuery(id+"F0.wireOp",EDGE,"E219"),sQuery(id+"F0.wireOp",EDGE,"E220"),sQuery(id+"F0.wireOp",EDGE,"E221"),sQuery(id+"F0.wireOp",EDGE,"E222"),sQuery(id+"F0.wireOp",EDGE,"E223"),sQuery(id+"F0.wireOp",EDGE,"E224"),sQuery(id+"F0.wireOp",EDGE,"E225"),sQuery(id+"F0.wireOp",EDGE,"E226"),sQuery(id+"F0.wireOp",EDGE,"E227"),sQuery(id+"F0.wireOp",EDGE,"E228"),sQuery(id+"F0.wireOp",EDGE,"E229"),sQuery(id+"F0.wireOp",EDGE,"E230"),sQuery(id+"F0.wireOp",EDGE,"E231"),sQuery(id+"F0.wireOp",EDGE,"E233"),sQuery(id+"F0.wireOp",EDGE,"E234"),sQuery(id+"F0.wireOp",EDGE,"E235"),sQuery(id+"F0.wireOp",EDGE,"E236")])],"isStart":true});
            var sketch = newSketch(context, id + "F2", { "sketchPlane" : qUnion([Q0])});
            skLineSegment(sketch, "E238.bottom", {"start": v(95.46, -41.16) * mm, "end": v(-95.46, -41.16) * mm, "construction": true});
            skLineSegment(sketch, "E238.top", {"start": v(95.46, 41.16) * mm, "end": v(-95.46, 41.16) * mm, "construction": true});
            skLineSegment(sketch, "E238.left", {"start": v(95.46, -41.16) * mm, "end": v(95.46, 41.16) * mm, "construction": true});
            skLineSegment(sketch, "E238.right", {"start": v(-95.46, -41.16) * mm, "end": v(-95.46, 41.16) * mm, "construction": true});
            skPoint(sketch, "E238.middle", {"position": v(0, 0) * mm});
            skCircle(sketch, "E239", {"center": v(95.46, -41.16) * mm, "radius": 1.5 * mm});
            skCircle(sketch, "E240", {"center": v(95.46, 0) * mm, "radius": 1.5 * mm});
            skCircle(sketch, "E241", {"center": v(95.46, 41.16) * mm, "radius": 1.5 * mm});
            skCircle(sketch, "E242", {"center": v(0, 41.16) * mm, "radius": 1.5 * mm});
            skCircle(sketch, "E243", {"center": v(-95.46, 41.16) * mm, "radius": 1.5 * mm});
            skCircle(sketch, "E244", {"center": v(-95.46, 0) * mm, "radius": 1.5 * mm});
            skCircle(sketch, "E245", {"center": v(-95.46, -41.16) * mm, "radius": 1.5 * mm});
            skCircle(sketch, "E246", {"center": v(0, -41.16) * mm, "radius": 1.5 * mm});
            skCircle(sketch, "E247", {"center": v(95.46, -41.16) * mm, "radius": 0.45 * mm});
            skCircle(sketch, "E248", {"center": v(95.46, 0) * mm, "radius": 0.45 * mm});
            skCircle(sketch, "E249", {"center": v(95.46, 41.16) * mm, "radius": 0.45 * mm});
            skCircle(sketch, "E250", {"center": v(0, 41.16) * mm, "radius": 0.45 * mm});
            skCircle(sketch, "E251", {"center": v(-95.46, 41.16) * mm, "radius": 0.45 * mm});
            skCircle(sketch, "E252", {"center": v(-95.46, 0) * mm, "radius": 0.45 * mm});
            skCircle(sketch, "E253", {"center": v(-95.46, -41.16) * mm, "radius": 0.45 * mm});
            skCircle(sketch, "E254", {"center": v(0, -41.16) * mm, "radius": 0.45 * mm});
            skSolve(sketch);
        }
        {
            var Q0;
            Q0=makeQuery(id+"F2.imprint","IMPRINT",FACE,{"disambiguationData":[TD([[makeQuery(id+"F2.imprint","IMPRINT",EDGE,{"derivedFrom":sQuery(id+"F2.wireOp",EDGE,"E239")}),1.0]])]});
            var Q1;
            Q1=makeQuery(id+"F2.imprint","IMPRINT",FACE,{"disambiguationData":[TD([[makeQuery(id+"F2.imprint","IMPRINT",EDGE,{"derivedFrom":sQuery(id+"F2.wireOp",EDGE,"E240")}),1.0]])]});
            var Q2;
            Q2=makeQuery(id+"F2.imprint","IMPRINT",FACE,{"disambiguationData":[TD([[makeQuery(id+"F2.imprint","IMPRINT",EDGE,{"derivedFrom":sQuery(id+"F2.wireOp",EDGE,"E241")}),1.0]])]});
            var Q3;
            Q3=makeQuery(id+"F2.imprint","IMPRINT",FACE,{"disambiguationData":[TD([[makeQuery(id+"F2.imprint","IMPRINT",EDGE,{"derivedFrom":sQuery(id+"F2.wireOp",EDGE,"E242")}),1.0]])]});
            var Q4;
            Q4=makeQuery(id+"F2.imprint","IMPRINT",FACE,{"disambiguationData":[TD([[makeQuery(id+"F2.imprint","IMPRINT",EDGE,{"derivedFrom":sQuery(id+"F2.wireOp",EDGE,"E243")}),1.0]])]});
            var Q5;
            Q5=makeQuery(id+"F2.imprint","IMPRINT",FACE,{"disambiguationData":[TD([[makeQuery(id+"F2.imprint","IMPRINT",EDGE,{"derivedFrom":sQuery(id+"F2.wireOp",EDGE,"E244")}),1.0]])]});
            var Q6;
            Q6=makeQuery(id+"F2.imprint","IMPRINT",FACE,{"disambiguationData":[TD([[makeQuery(id+"F2.imprint","IMPRINT",EDGE,{"derivedFrom":sQuery(id+"F2.wireOp",EDGE,"E245")}),1.0]])]});
            var Q7;
            Q7=makeQuery(id+"F2.imprint","IMPRINT",FACE,{"disambiguationData":[TD([[makeQuery(id+"F2.imprint","IMPRINT",EDGE,{"derivedFrom":sQuery(id+"F2.wireOp",EDGE,"E246")}),1.0]])]});
            extrude(context, id + "F3", {"entities" : qUnion([Q0, Q1, Q2, Q3, Q4, Q5, Q6, Q7]), "operationType" : NewBodyOperationType.ADD, "depth" : 0.7 * mm});
        }
        {
            var Q0;
            Q0=makeQuery(id+"F3.opExtrude","CAP_FACE",FACE,{"disambiguationData":[OSD([sQuery(id+"F2.wireOp",EDGE,"E243"),sQuery(id+"F2.wireOp",EDGE,"E251")])],"isStart":false});
            var sketch = newSketch(context, id + "F4", { "sketchPlane" : qUnion([Q0])});
            skLineSegment(sketch, "E255.bottom", {"start": v(-97.5, 43.25) * mm, "end": v(97.5, 43.25) * mm});
            skLineSegment(sketch, "E255.top", {"start": v(-97.5, -43.25) * mm, "end": v(97.5, -43.25) * mm});
            skLineSegment(sketch, "E255.left", {"start": v(-97.5, 43.25) * mm, "end": v(-97.5, -43.25) * mm});
            skLineSegment(sketch, "E255.right", {"start": v(97.5, 43.25) * mm, "end": v(97.5, -43.25) * mm});
            skPoint(sketch, "E255.middle", {"position": v(0, 0) * mm});
            skSolve(sketch);
        }
        {
            var Q0;
            Q0=makeQuery(id+"F4.imprint","IMPRINT",FACE,{"disambiguationData":[TD([[makeQuery(id+"F4.imprint","IMPRINT",EDGE,{"derivedFrom":sQuery(id+"F4.wireOp",EDGE,"E255.bottom")}),-1.0]])]});
            var Q1;
            Q1=makeQuery(id+"F4.imprint","IMPRINT",FACE,{"disambiguationData":[TD([[makeQuery(id+"F4.imprint","IMPRINT",EDGE,{"derivedFrom":makeQuery(id+"F3.opExtrude","CAP_EDGE",EDGE,{"disambiguationData":[OSD([sQuery(id+"F2.wireOp",EDGE,"E243")])],"isStart":false})}),1.0]])]});
            var Q2;
            Q2=makeQuery(id+"F4.imprint","IMPRINT",FACE,{"disambiguationData":[TD([[makeQuery(id+"F4.imprint","IMPRINT",EDGE,{"derivedFrom":makeQuery(id+"F3.opExtrude","CAP_EDGE",EDGE,{"disambiguationData":[OSD([sQuery(id+"F2.wireOp",EDGE,"E251")])],"isStart":false})}),1.0]])]});
            extrude(context, id + "F5", {"entities" : qUnion([Q0, Q1, Q2]), "depth" : 0.8 * mm});
        }
    });
